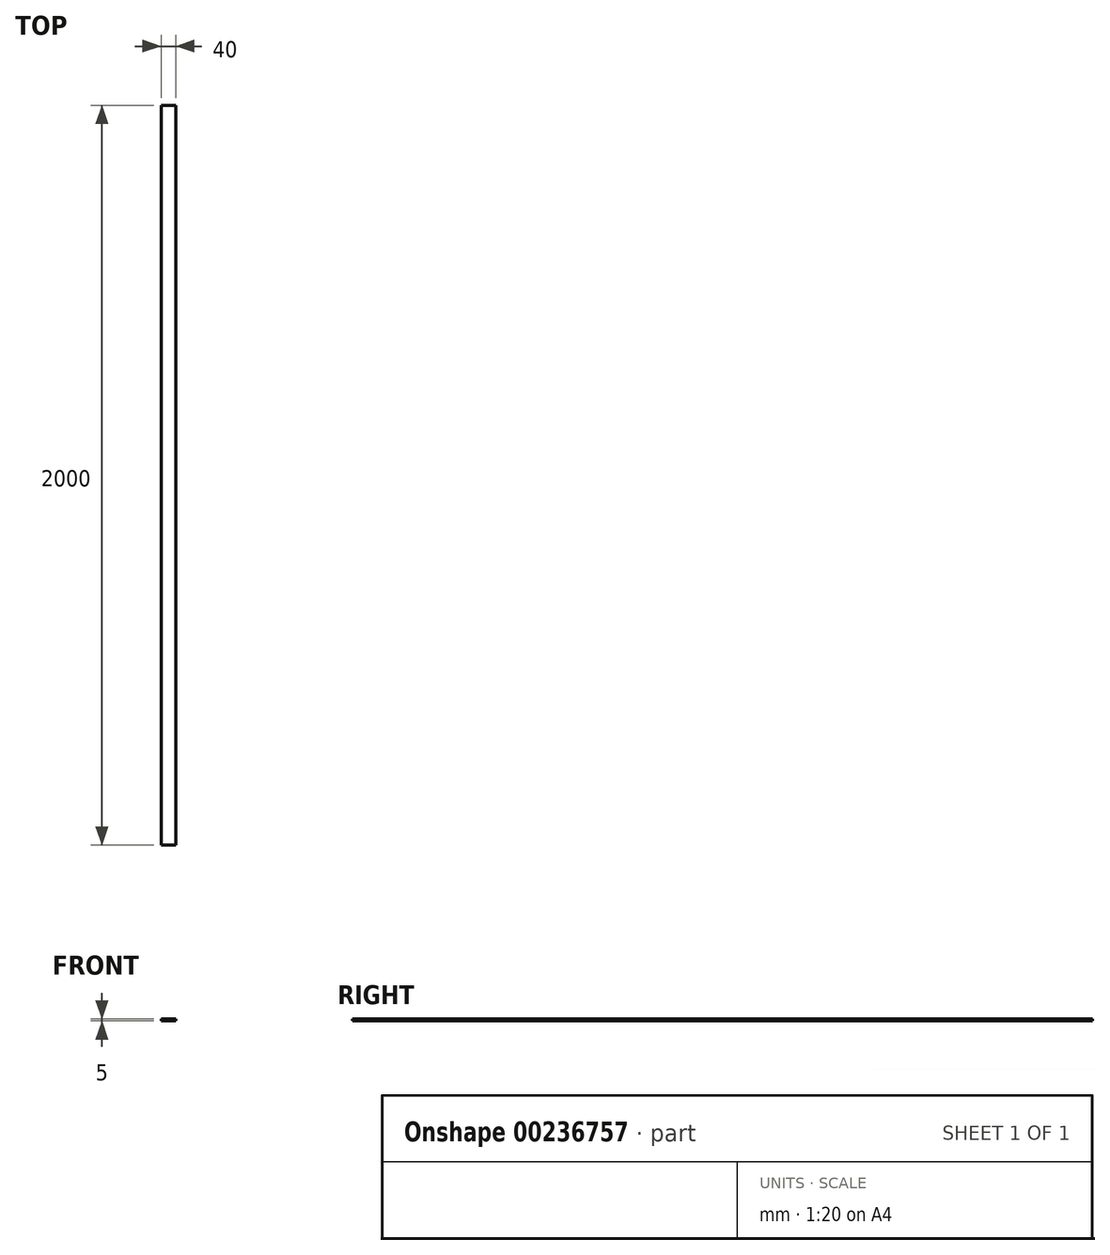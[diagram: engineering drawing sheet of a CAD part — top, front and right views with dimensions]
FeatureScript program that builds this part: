
annotation { "Feature Type Name" : "Feature", "Feature Type Description" : "" }
export const myFeature = defineFeature(function(context is Context, id is Id, definition is map)
    precondition{}
    {
        {
            var Q0;
            Q0=qCreatedBy(makeId("Front.planeOp"),FACE);
            var sketch = newSketch(context, id + "F0", { "sketchPlane" : qUnion([Q0])});
            skLineSegment(sketch, "E0.bottom", {"start": v(0, 0) * mm, "end": v(40, 0) * mm});
            skLineSegment(sketch, "E0.top", {"start": v(0, 5) * mm, "end": v(40, 5) * mm});
            skLineSegment(sketch, "E0.left", {"start": v(0, 0) * mm, "end": v(0, 5) * mm});
            skLineSegment(sketch, "E0.right", {"start": v(40, 0) * mm, "end": v(40, 5) * mm});
            skSolve(sketch);
        }
        {
            var Q0;
            Q0=makeQuery(id+"F0.imprint","IMPRINT",FACE,{"disambiguationData":[TD([[makeQuery(id+"F0.imprint","IMPRINT",EDGE,{"derivedFrom":sQuery(id+"F0.wireOp",EDGE,"E0.bottom")}),1.0]])]});
            extrude(context, id + "F1", {"entities" : qUnion([Q0]), "depth" : 2000 * mm, "offsetDistance" : 25 * mm});
        }
    });
